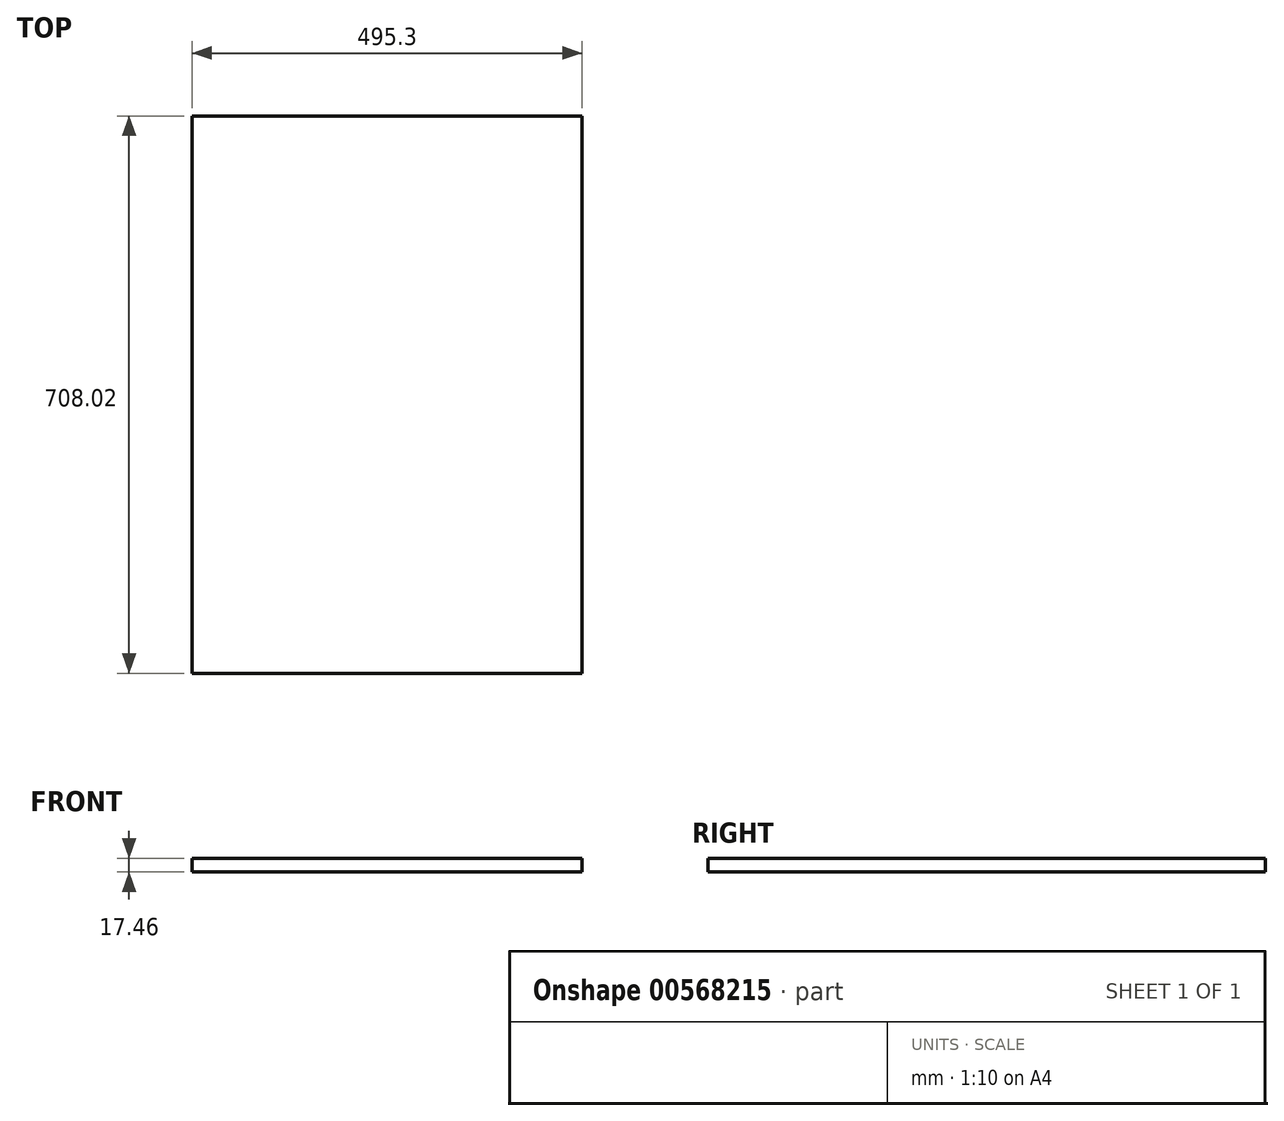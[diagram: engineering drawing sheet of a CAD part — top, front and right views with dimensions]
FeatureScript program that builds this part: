
annotation { "Feature Type Name" : "Feature", "Feature Type Description" : "" }
export const myFeature = defineFeature(function(context is Context, id is Id, definition is map)
    precondition{}
    {
        {
            var Q0;
            Q0=qCreatedBy(makeId("Top.planeOp"),FACE);
            var sketch = newSketch(context, id + "F0", { "sketchPlane" : qUnion([Q0])});
            skLineSegment(sketch, "E0.bottom", {"start": v(0, 0) * mm, "end": v(495.3, 0) * mm});
            skLineSegment(sketch, "E0.top", {"start": v(0, 708.02) * mm, "end": v(495.3, 708.02) * mm});
            skLineSegment(sketch, "E0.left", {"start": v(0, 0) * mm, "end": v(0, 708.02) * mm});
            skLineSegment(sketch, "E0.right", {"start": v(495.3, 0) * mm, "end": v(495.3, 708.03) * mm});
            skSolve(sketch);
        }
        {
            var Q0;
            Q0=makeQuery(id+"F0.imprint","IMPRINT",FACE,{"disambiguationData":[TD([[makeQuery(id+"F0.imprint","IMPRINT",EDGE,{"derivedFrom":sQuery(id+"F0.wireOp",EDGE,"E0.bottom")}),1.0]])]});
            extrude(context, id + "F1", {"entities" : qUnion([Q0]), "depth" : 17.46 * mm, "offsetDistance" : 25.4 * mm});
        }
    });
